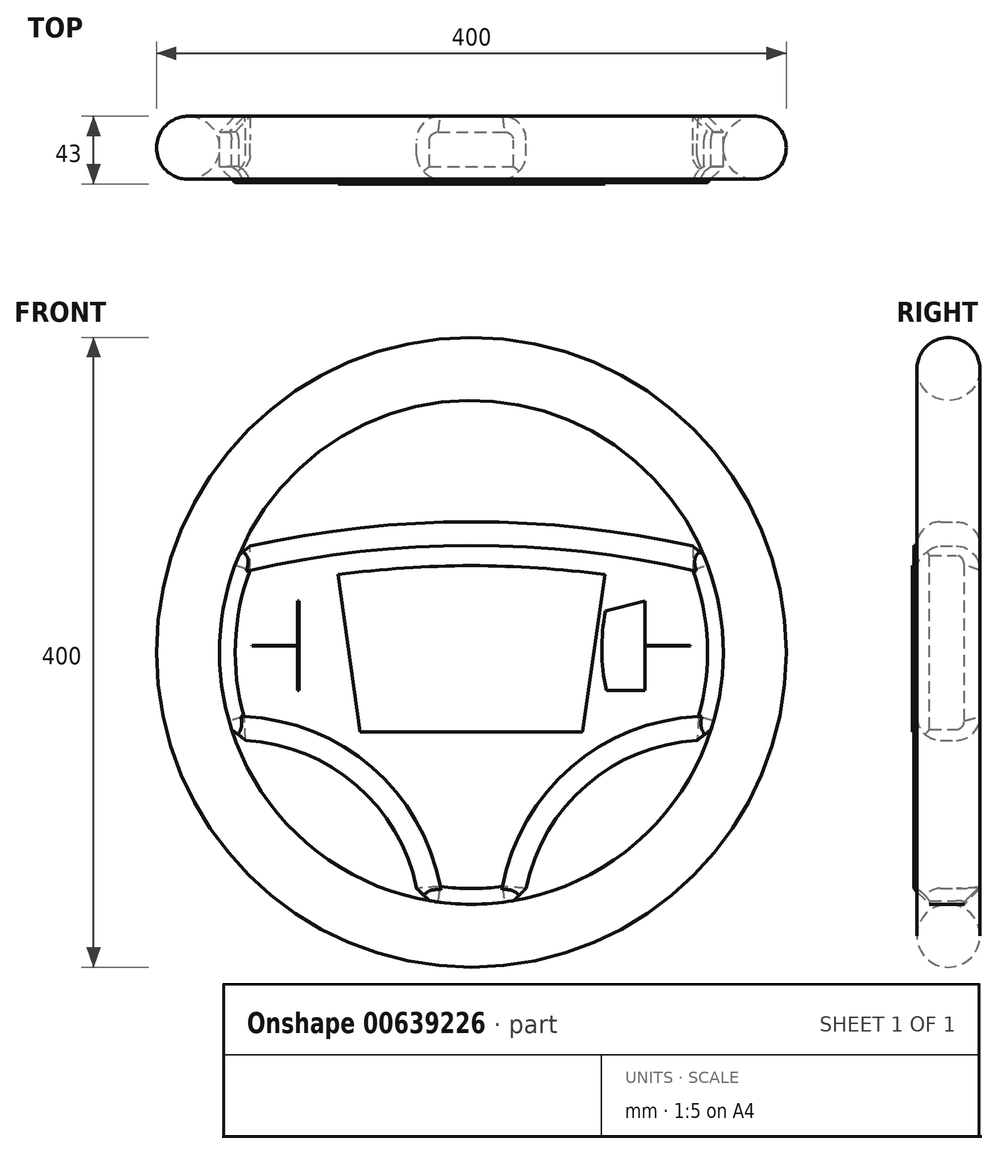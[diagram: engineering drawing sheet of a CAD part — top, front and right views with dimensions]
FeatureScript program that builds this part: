
annotation { "Feature Type Name" : "Feature", "Feature Type Description" : "" }
export const myFeature = defineFeature(function(context is Context, id is Id, definition is map)
    precondition{}
    {
        {
            var Q0;
            Q0=qCreatedBy(makeId("Front.planeOp"),FACE);
            var sketch = newSketch(context, id + "F0", { "sketchPlane" : qUnion([Q0])});
            skCircle(sketch, "E0", {"center": v(0, 0) * mm, "radius": 200 * mm});
            skCircle(sketch, "E1", {"center": v(0, 0) * mm, "radius": 160 * mm});
            skArc(sketch, "E2", {"start": v(145.57, 66.4) * mm, "mid": v(0, 82.9) * mm, "end": v(-145.57, 66.4) * mm});
            skArc(sketch, "E3", {"start": v(-33.63, -156.43) * mm, "mid": v(-73.04, -84.38) * mm, "end": v(-149.99, -55.7) * mm});
            skArc(sketch, "E4.MirrorCS", {"start": v(33.63, -156.43) * mm, "mid": v(73.04, -84.38) * mm, "end": v(149.99, -55.7) * mm});
            skSolve(sketch);
        }
        {
            var Q0;
            Q0=makeQuery(id+"F0.imprint","IMPRINT",FACE,{"disambiguationData":[TD([[makeQuery(id+"F0.imprint","IMPRINT",EDGE,{"derivedFrom":sQuery(id+"F0.wireOp",EDGE,"E0")}),1.0]])]});
            extrude(context, id + "F1", {"entities" : qUnion([Q0]), "depth" : 40 * mm, "offsetDistance" : 25 * mm});
        }
        {
            var Q0;
            Q0=makeQuery(id+"F1.opExtrude","CAP_EDGE",EDGE,{"disambiguationData":[OSD([sQuery(id+"F0.wireOp",EDGE,"E0")])],"isStart":false});
            var Q1;
            Q1=makeQuery(id+"F1.opExtrude","CAP_EDGE",EDGE,{"disambiguationData":[OSD([sQuery(id+"F0.wireOp",EDGE,"E1")])],"isStart":false});
            var Q2;
            Q2=makeQuery(id+"F1.opExtrude","CAP_EDGE",EDGE,{"disambiguationData":[OSD([sQuery(id+"F0.wireOp",EDGE,"E0")])],"isStart":true});
            var Q3;
            Q3=makeQuery(id+"F1.opExtrude","CAP_EDGE",EDGE,{"disambiguationData":[OSD([sQuery(id+"F0.wireOp",EDGE,"E1")])],"isStart":true});
            fillet(context, id + "F2", {"entities" : qUnion([Q0, Q1, Q2, Q3]), "radius" : 20 * mm, "tangentPropagation" : true, "allowEdgeOverflow" : false});
        }
        {
            var Q0;
            {var subQ0=sQuery(id+"F0.wireOp",EDGE,"E2");Q0=makeQuery(id+"F0.imprint","IMPRINT",FACE,{"disambiguationData":[TD([[makeQuery(id+"F0.imprint","IMPRINT",EDGE,{"derivedFrom":subQ0}),1.0]])]});}
            extrude(context, id + "F3", {"entities" : qUnion([Q0]), "operationType" : NewBodyOperationType.ADD, "depth" : 40 * mm, "offsetDistance" : 25 * mm});
        }
        {
            var Q0;
            Q0=makeQuery(id+"F3.opExtrude","CAP_EDGE",EDGE,{"disambiguationData":[OSD([sQuery(id+"F0.wireOp",EDGE,"E2")])],"isStart":true});
            var Q1;
            Q1=makeQuery(id+"F3.opExtrude","CAP_EDGE",EDGE,{"disambiguationData":[OSD([sQuery(id+"F0.wireOp",EDGE,"E4.MirrorCS")])],"isStart":true});
            var Q2;
            Q2=makeQuery(id+"F3.opExtrude","CAP_EDGE",EDGE,{"disambiguationData":[OSD([sQuery(id+"F0.wireOp",EDGE,"E3")])],"isStart":true});
            var Q3;
            Q3=makeQuery(id+"F3.opExtrude","CAP_EDGE",EDGE,{"disambiguationData":[OSD([sQuery(id+"F0.wireOp",EDGE,"E2")])],"isStart":false});
            var Q4;
            Q4=makeQuery(id+"F3.opExtrude","CAP_EDGE",EDGE,{"disambiguationData":[OSD([sQuery(id+"F0.wireOp",EDGE,"E4.MirrorCS")])],"isStart":false});
            var Q5;
            Q5=makeQuery(id+"F3.opExtrude","CAP_EDGE",EDGE,{"disambiguationData":[OSD([sQuery(id+"F0.wireOp",EDGE,"E3")])],"isStart":false});
            fillet(context, id + "F4", {"entities" : qUnion([Q0, Q1, Q2, Q3, Q4, Q5]), "radius" : 15 * mm, "tangentPropagation" : true, "allowEdgeOverflow" : false});
        }
        {
            var Q0;
            Q0=makeQuery(id+"F3.opExtrude","CAP_FACE",FACE,{"disambiguationData":[OSD([sQuery(id+"F0.wireOp",EDGE,"E1"),sQuery(id+"F0.wireOp",EDGE,"E2"),sQuery(id+"F0.wireOp",EDGE,"E3"),sQuery(id+"F0.wireOp",EDGE,"E4.MirrorCS")])],"isStart":false});
            var sketch = newSketch(context, id + "F5", { "sketchPlane" : qUnion([Q0])});
            skLineSegment(sketch, "E5", {"start": v(0, 92.8) * mm, "end": v(0, -79.06) * mm, "construction": true});
            skArc(sketch, "E6", {"start": v(-135.3, 39.3) * mm, "mid": v(-139.24, 7.54) * mm, "end": v(-134.64, -24.14) * mm});
            skArc(sketch, "E7", {"start": v(-85.71, -24.14) * mm, "mid": v(-82.84, 1) * mm, "end": v(-85.3, 26.2) * mm});
            skLineSegment(sketch, "E8", {"start": v(-134.64, -24.14) * mm, "end": v(-85.71, -24.14) * mm});
            skLineSegment(sketch, "E9", {"start": v(-135.3, 39.3) * mm, "end": v(-85.3, 26.2) * mm});
            skArc(sketch, "E10.MirrorCS", {"start": v(85.71, -24.14) * mm, "mid": v(82.84, 1) * mm, "end": v(85.3, 26.2) * mm});
            skLineSegment(sketch, "E11.MirrorCS", {"start": v(135.3, 39.3) * mm, "end": v(85.3, 26.2) * mm});
            skArc(sketch, "E12.MirrorCS", {"start": v(135.3, 39.3) * mm, "mid": v(139.24, 7.54) * mm, "end": v(134.64, -24.14) * mm});
            skLineSegment(sketch, "E13.MirrorCS", {"start": v(134.64, -24.14) * mm, "end": v(85.71, -24.14) * mm});
            skLineSegment(sketch, "E14", {"start": v(-110.3, 32.76) * mm, "end": v(-110.3, -24.14) * mm});
            skLineSegment(sketch, "E15", {"start": v(-110.3, 4.3) * mm, "end": v(-139.17, 4.3) * mm});
            skLineSegment(sketch, "E16", {"start": v(-139.15, 3.96) * mm, "end": v(-110.3, 3.96) * mm});
            skLineSegment(sketch, "E17", {"start": v(-109.5, 32.54) * mm, "end": v(-109.5, -24.14) * mm});
            skLineSegment(sketch, "E18.MirrorCS", {"start": v(109.5, 32.54) * mm, "end": v(109.5, -24.14) * mm});
            skLineSegment(sketch, "E19.MirrorCS", {"start": v(110.3, 32.76) * mm, "end": v(110.3, -24.14) * mm});
            skLineSegment(sketch, "E20.MirrorCS", {"start": v(110.3, 4.3) * mm, "end": v(139.17, 4.3) * mm});
            skLineSegment(sketch, "E21.MirrorCS", {"start": v(139.15, 3.96) * mm, "end": v(110.3, 3.96) * mm});
            skArc(sketch, "E22", {"start": v(0, 55.17) * mm, "mid": v(-42.5, 53.54) * mm, "end": v(-84.8, 49.37) * mm});
            skLineSegment(sketch, "E23", {"start": v(-84.8, 49.37) * mm, "end": v(-70.67, -50.6) * mm});
            skLineSegment(sketch, "E24", {"start": v(-70.67, -50.6) * mm, "end": v(0, -50.6) * mm});
            skArc(sketch, "E25.MirrorCS", {"start": v(0, 55.17) * mm, "mid": v(42.5, 53.54) * mm, "end": v(84.8, 49.37) * mm});
            skLineSegment(sketch, "E26.MirrorCS", {"start": v(84.8, 49.37) * mm, "end": v(70.67, -50.6) * mm});
            skLineSegment(sketch, "E27.MirrorCS", {"start": v(70.67, -50.6) * mm, "end": v(0, -50.6) * mm});
            skSolve(sketch);
        }
        {
            var Q0;
            {var subQ3=sQuery(id+"F5.wireOp",EDGE,"E15");Q0=makeQuery(id+"F5.imprint","IMPRINT",FACE,{"disambiguationData":[TD([[makeQuery(id+"F5.imprint","IMPRINT",EDGE,{"derivedFrom":subQ3}),-1.0]])]});}
            var Q1;
            {var subQ3=sQuery(id+"F5.wireOp",EDGE,"E16");Q1=makeQuery(id+"F5.imprint","IMPRINT",FACE,{"disambiguationData":[TD([[makeQuery(id+"F5.imprint","IMPRINT",EDGE,{"derivedFrom":subQ3}),-1.0]])]});}
            var Q2;
            {var subQ0=sQuery(id+"F5.wireOp",EDGE,"E7");Q2=makeQuery(id+"F5.imprint","IMPRINT",FACE,{"disambiguationData":[TD([[makeQuery(id+"F5.imprint","IMPRINT",EDGE,{"derivedFrom":subQ0}),1.0]])]});}
            var Q3;
            {var subQ0=sQuery(id+"F5.wireOp",EDGE,"E10.MirrorCS");Q3=makeQuery(id+"F5.imprint","IMPRINT",FACE,{"disambiguationData":[TD([[makeQuery(id+"F5.imprint","IMPRINT",EDGE,{"derivedFrom":subQ0}),-1.0]])]});}
            var Q4;
            {var subQ5=sQuery(id+"F5.wireOp",EDGE,"E20.MirrorCS");Q4=makeQuery(id+"F5.imprint","IMPRINT",FACE,{"disambiguationData":[TD([[makeQuery(id+"F5.imprint","IMPRINT",EDGE,{"derivedFrom":subQ5}),1.0]])]});}
            var Q5;
            {var subQ3=sQuery(id+"F5.wireOp",EDGE,"E21.MirrorCS");Q5=makeQuery(id+"F5.imprint","IMPRINT",FACE,{"disambiguationData":[TD([[makeQuery(id+"F5.imprint","IMPRINT",EDGE,{"derivedFrom":subQ3}),1.0]])]});}
            extrude(context, id + "F6", {"entities" : qUnion([Q0, Q1, Q2, Q3, Q4, Q5]), "operationType" : NewBodyOperationType.ADD, "depth" : 2 * mm, "offsetDistance" : 25 * mm});
        }
        {
            var Q0;
            Q0=makeQuery(id+"F5.imprint","IMPRINT",FACE,{"disambiguationData":[TD([[makeQuery(id+"F5.imprint","IMPRINT",EDGE,{"derivedFrom":sQuery(id+"F5.wireOp",EDGE,"E22")}),1.0]])]});
            extrude(context, id + "F7", {"entities" : qUnion([Q0]), "operationType" : NewBodyOperationType.ADD, "depth" : 3 * mm, "offsetDistance" : 25 * mm});
        }
        {
            var Q0;
            {var subQ0=sQuery(id+"F0.wireOp",EDGE,"E1");Q0=makeQuery(id+"F3.opExtrude","SWEPT_FACE",FACE,{"disambiguationData":[OSD([subQ0]),TDD([makeQuery(id+"F0.imprint","IMPRINT",EDGE,{"disambiguationData":[TD([[makeQuery(id+"F0.imprint","INTERSECT",VERTEX,{"disambiguationData":[OD(0.0)],"derivedFrom":[subQ0,sQuery(id+"F0.wireOp",EDGE,"E3")]}),-1.0]])],"derivedFrom":subQ0})])]});}
            var Q1;
            {var subQ0=sQuery(id+"F0.wireOp",EDGE,"E1");Q1=makeQuery(id+"F3.opExtrude","SWEPT_FACE",FACE,{"disambiguationData":[OSD([subQ0]),TDD([makeQuery(id+"F0.imprint","IMPRINT",EDGE,{"disambiguationData":[TD([[makeQuery(id+"F0.imprint","INTERSECT",VERTEX,{"disambiguationData":[OD(0.0)],"derivedFrom":[subQ0,sQuery(id+"F0.wireOp",EDGE,"E2")]}),1.0]])],"derivedFrom":subQ0})])]});}
            var Q2;
            {var subQ0=sQuery(id+"F0.wireOp",EDGE,"E1");Q2=makeQuery(id+"F3.opExtrude","SWEPT_FACE",FACE,{"disambiguationData":[OSD([subQ0]),TDD([makeQuery(id+"F0.imprint","IMPRINT",EDGE,{"disambiguationData":[TD([[makeQuery(id+"F0.imprint","INTERSECT",VERTEX,{"disambiguationData":[OD(1.0)],"derivedFrom":[subQ0,sQuery(id+"F0.wireOp",EDGE,"E2")]}),-1.0]])],"derivedFrom":subQ0})])]});}
            chamfer(context, id + "F8", {"entities" : qUnion([Q0, Q1, Q2]), "width" : 10 * mm, "tangentPropagation" : true});
        }
    });
